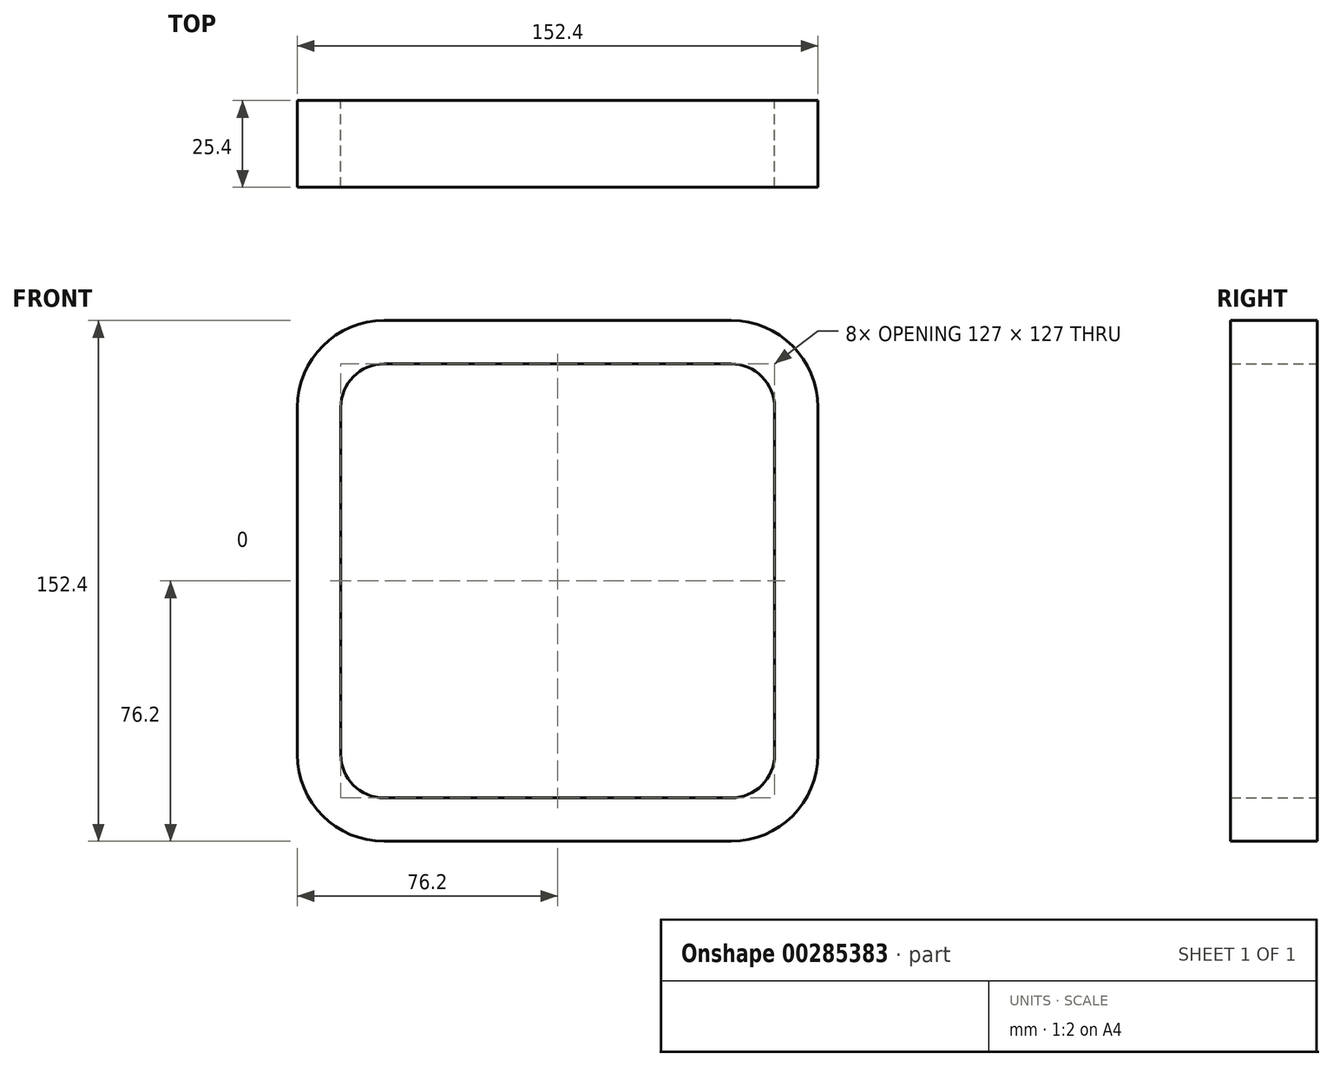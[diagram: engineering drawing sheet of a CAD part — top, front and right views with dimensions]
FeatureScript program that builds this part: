
annotation { "Feature Type Name" : "Feature", "Feature Type Description" : "" }
export const myFeature = defineFeature(function(context is Context, id is Id, definition is map)
    precondition{}
    {
        {
            var Q0;
            Q0=qCreatedBy(makeId("Front.planeOp"),FACE);
            var sketch = newSketch(context, id + "F0", { "sketchPlane" : qUnion([Q0])});
            skLineSegment(sketch, "E0.bottom", {"start": v(50.8, 76.2) * mm, "end": v(-50.8, 76.2) * mm});
            skLineSegment(sketch, "E0.top", {"start": v(50.8, -76.2) * mm, "end": v(-50.8, -76.2) * mm});
            skLineSegment(sketch, "E0.left", {"start": v(76.2, 50.8) * mm, "end": v(76.2, -50.8) * mm});
            skLineSegment(sketch, "E0.right", {"start": v(-76.2, 50.8) * mm, "end": v(-76.2, -50.8) * mm});
            skPoint(sketch, "E0.middle", {"position": v(0, 0) * mm});
            skLineSegment(sketch, "E1.bottom", {"start": v(50.8, 63.5) * mm, "end": v(-50.8, 63.5) * mm});
            skLineSegment(sketch, "E1.top", {"start": v(50.8, -63.5) * mm, "end": v(-50.8, -63.5) * mm});
            skLineSegment(sketch, "E1.left", {"start": v(63.5, 50.8) * mm, "end": v(63.5, -50.8) * mm});
            skLineSegment(sketch, "E1.right", {"start": v(-63.5, 50.8) * mm, "end": v(-63.5, -50.8) * mm});
            skPoint(sketch, "E2.visualSharp", {"position": v(-63.5, 63.5) * mm});
            skArc(sketch, "E2.filletArc", {"start": v(-50.8, 63.5) * mm, "mid": v(-59.78, 59.78) * mm, "end": v(-63.5, 50.8) * mm});
            skPoint(sketch, "E3.visualSharp", {"position": v(63.5, 63.5) * mm});
            skArc(sketch, "E3.filletArc", {"start": v(63.5, 50.8) * mm, "mid": v(59.78, 59.78) * mm, "end": v(50.8, 63.5) * mm});
            skPoint(sketch, "E4.visualSharp", {"position": v(63.5, -63.5) * mm});
            skArc(sketch, "E4.filletArc", {"start": v(50.8, -63.5) * mm, "mid": v(59.78, -59.78) * mm, "end": v(63.5, -50.8) * mm});
            skPoint(sketch, "E5.visualSharp", {"position": v(-63.5, -63.5) * mm});
            skArc(sketch, "E5.filletArc", {"start": v(-63.5, -50.8) * mm, "mid": v(-59.78, -59.78) * mm, "end": v(-50.8, -63.5) * mm});
            skPoint(sketch, "E6.visualSharp", {"position": v(-76.2, 76.2) * mm});
            skArc(sketch, "E6.filletArc", {"start": v(-50.8, 76.2) * mm, "mid": v(-68.76, 68.76) * mm, "end": v(-76.2, 50.8) * mm});
            skPoint(sketch, "E7.visualSharp", {"position": v(76.2, 76.2) * mm});
            skArc(sketch, "E7.filletArc", {"start": v(76.2, 50.8) * mm, "mid": v(68.76, 68.76) * mm, "end": v(50.8, 76.2) * mm});
            skPoint(sketch, "E8.visualSharp", {"position": v(76.2, -76.2) * mm});
            skArc(sketch, "E8.filletArc", {"start": v(50.8, -76.2) * mm, "mid": v(68.76, -68.76) * mm, "end": v(76.2, -50.8) * mm});
            skPoint(sketch, "E9.visualSharp", {"position": v(-76.2, -76.2) * mm});
            skArc(sketch, "E9.filletArc", {"start": v(-76.2, -50.8) * mm, "mid": v(-68.76, -68.76) * mm, "end": v(-50.8, -76.2) * mm});
            skLineSegment(sketch, "E10", {"start": v(0, 76.2) * mm, "end": v(0, 63.5) * mm, "construction": true});
            skLineSegment(sketch, "E11", {"start": v(63.5, 0) * mm, "end": v(76.2, 0) * mm, "construction": true});
            skLineSegment(sketch, "E12", {"start": v(50.8, 50.8) * mm, "end": v(63.5, 50.8) * mm, "construction": true});
            skSolve(sketch);
        }
        {
            var Q0;
            Q0 = qSketchRegion(id + "F0", true);
            extrude(context, id + "F1", {"entities" : qUnion([Q0]), "depth" : 25.4 * mm});
        }
    });
